# Revit family: Hand_Dryer-Excel_Dryer-XLERATOReco_Unit
name_source: partatom
category: Specialty Equipment
revit_build: Autodesk Revit 2017 (Build: 20190508_0315(x64)
units: mm (PartAtom-declared; Revit-internal decimal feet)

## family parameters
Cut with Voids When Loaded = No
Host = Face
OmniClass Number = 23.40.20.21.14
OmniClass Title = Hand and Hair Dryers
Part Type = Normal
Room Calculation Point = No
Round Connector Dimension = Use Diameter
Shared = No

## types (4) — shared parameters
ADA Compliance = http://www.exceldryer.com
Apparent Load = 500 VA
Assembly Code = C1030200
Cost Information = http://www.exceldryer.com
Cost Savings Analysis = http://www.exceldryer.com
Cover Finish = Bulk Molding Compound - Excel Dryer - Thermoset Resin - White
Cover Material = Thermoset Resin
Default Elevation = 3' - 5"
Depth = 0' - 6 7/8"
Description = XLERATOReco Hand Dryer
Dry Time = 10-15 Seconds
Expected Lifespan = 15+ Years
Green Building LEED = http://www.exceldryer.com
Height = 1' - 0 7/8"
Impact Resistant Note = UL 499
Installation Phase = Single
Installation URL = http://www.exceldryer.com
Keynote = 10 28 13
Maintenance Schedule = Once to Twice per Year
Manufacturer = Excel Dryer
Manufacturer Fax Number = 1-413-525-2853
Model = XL-BW-ECO
Motor Note = 2-4.5 Amps
Number of Poles = 1
Output at Outlet (LFM) = 16000
Phase = 1
Power Factor = 1
Product Documentation Link = http://www.exceldryer.com
Product Name = XLERATOReco Hand Dryer
Product Page URL = http://www.exceldryer.com
Product Weight = 17lbs
Run-Time Cycle = Automatic
Time Cycle = Automatic
URL = http://www.exceldryer.com
Version = 2017 - v1.0b
Void = 0' - 0 1/16"
Void Depth = 6' - 7 15/16"
Warranty Duration = 5 Years
Warranty URL = https://www.exceldryer.com
Watts = 500 W
Width = 0' - 11 15/16"

## per-type parameters (varying)
| type | Amperage | Frequency | Voltage |
| XL-BW-ECO-ECO-120V | 13 A | 60 Hz | 120 V |
| XL-BW-ECO-ECO-208V | 7 A | 60 Hz | 208 V |
| XL-BW-ECO-ECO-240V | 7 A | 60 Hz | 240 V |
| XL-BW-ECO-ECO-230V | 7 A | 50 Hz | 230 V |

## geometry (parser evidence)
native form markers: Sweep x2
no freeform markers — native parametric forms only
